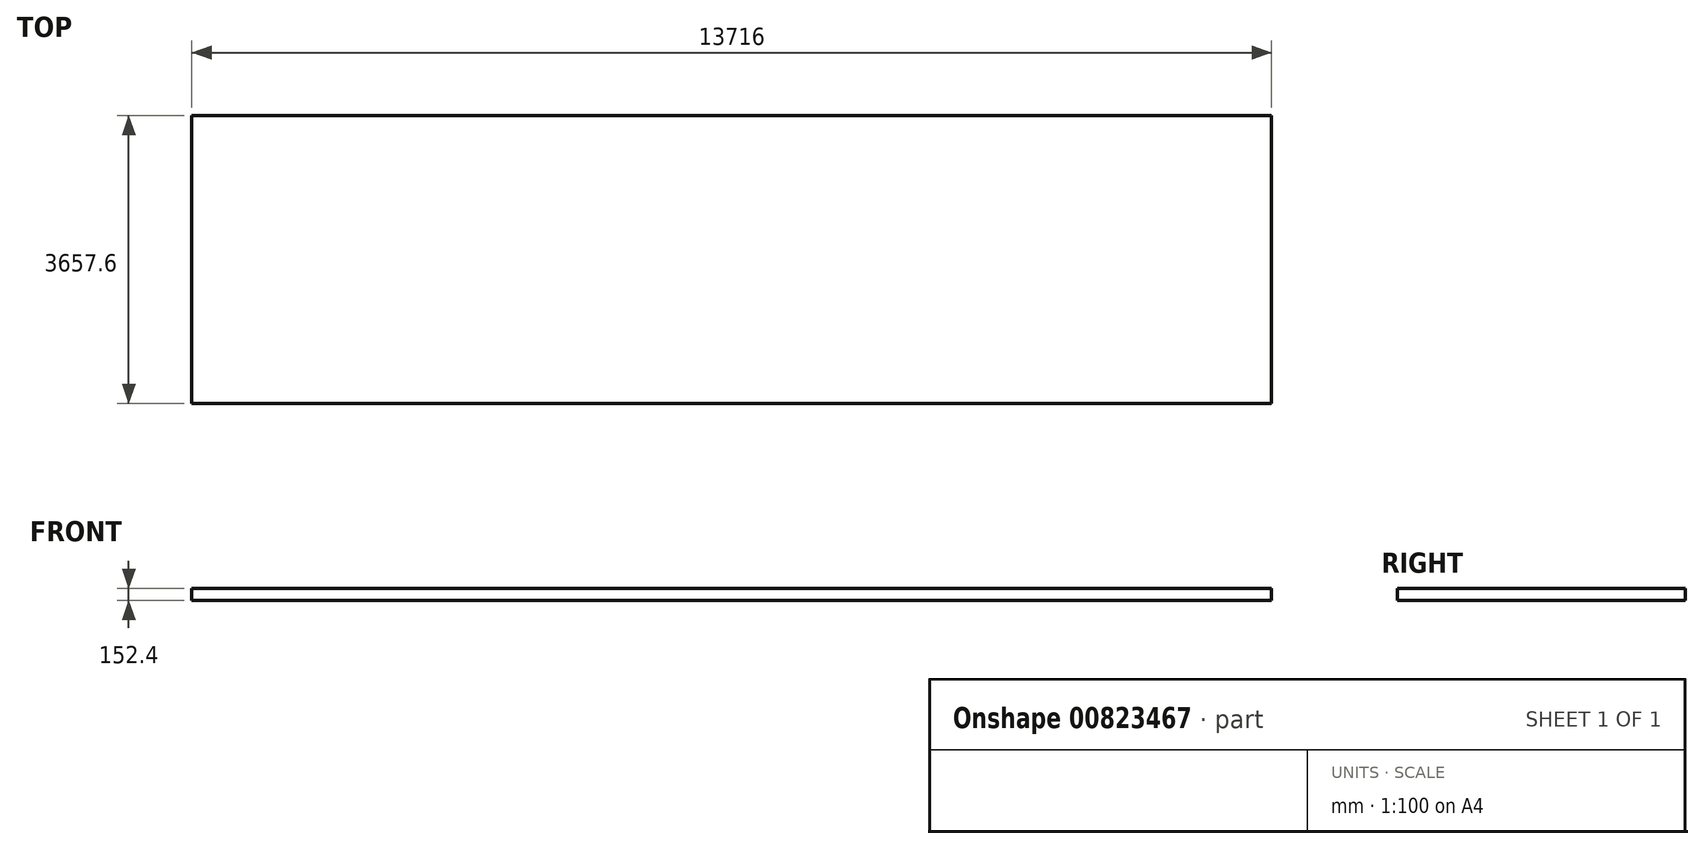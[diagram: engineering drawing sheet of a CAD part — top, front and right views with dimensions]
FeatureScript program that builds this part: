
annotation { "Feature Type Name" : "Feature", "Feature Type Description" : "" }
export const myFeature = defineFeature(function(context is Context, id is Id, definition is map)
    precondition{}
    {
        {
            var Q0;
            Q0=qCreatedBy(makeId("Top.planeOp"),FACE);
            var sketch = newSketch(context, id + "F0", { "sketchPlane" : qUnion([Q0])});
            skLineSegment(sketch, "E0.bottom", {"start": v(6858, 1828.8) * mm, "end": v(-6858, 1828.8) * mm});
            skLineSegment(sketch, "E0.top", {"start": v(6858, -1828.8) * mm, "end": v(-6858, -1828.8) * mm});
            skLineSegment(sketch, "E0.left", {"start": v(6858, 1828.8) * mm, "end": v(6858, -1828.8) * mm});
            skLineSegment(sketch, "E0.right", {"start": v(-6858, 1828.8) * mm, "end": v(-6858, -1828.8) * mm});
            skPoint(sketch, "E0.middle", {"position": v(0, 0) * mm});
            skSolve(sketch);
        }
        {
            var Q0;
            Q0 = qSketchRegion(id + "F0", true);
            extrude(context, id + "F1", {"entities" : qUnion([Q0]), "depth" : 152.4 * mm, "offsetDistance" : 25.4 * mm});
        }
    });
